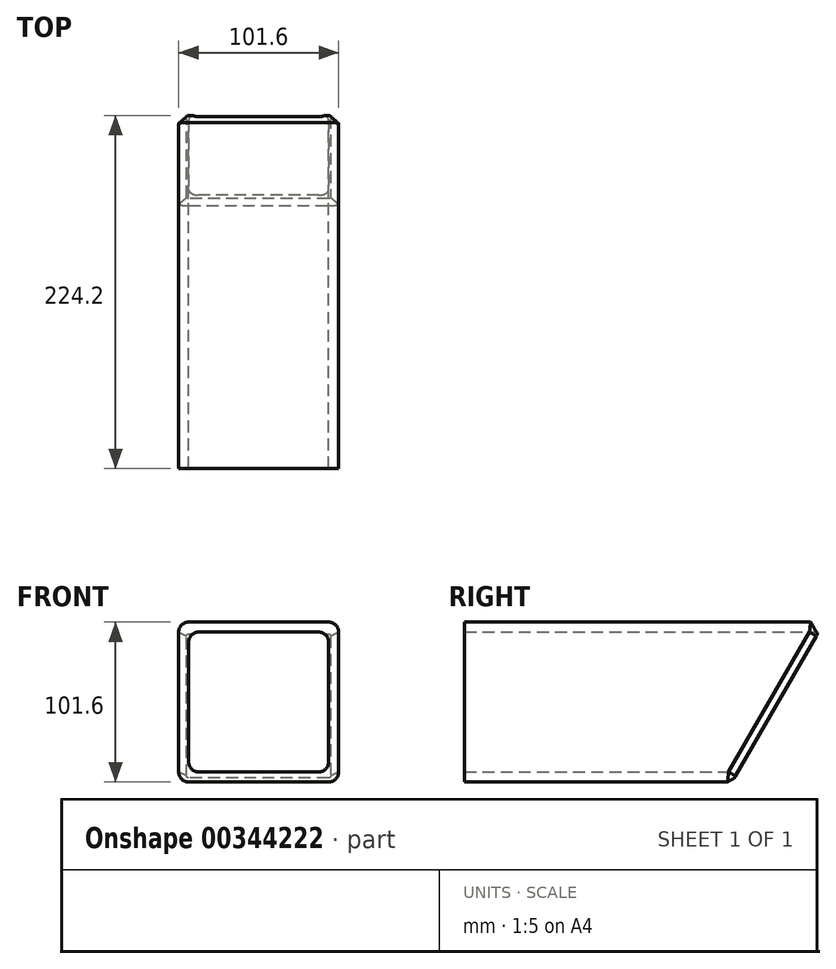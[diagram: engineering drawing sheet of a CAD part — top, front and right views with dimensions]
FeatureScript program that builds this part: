
annotation { "Feature Type Name" : "Feature", "Feature Type Description" : "" }
export const myFeature = defineFeature(function(context is Context, id is Id, definition is map)
    precondition{}
    {
        {
            var Q0;
            Q0=qCreatedBy(makeId("Front.planeOp"),FACE);
            var sketch = newSketch(context, id + "F0", { "sketchPlane" : qUnion([Q0])});
            skLineSegment(sketch, "E0.bottom", {"start": v(44.45, 50.8) * mm, "end": v(-44.45, 50.8) * mm});
            skLineSegment(sketch, "E0.top", {"start": v(44.45, -50.8) * mm, "end": v(-44.45, -50.8) * mm});
            skLineSegment(sketch, "E0.left", {"start": v(50.8, 44.45) * mm, "end": v(50.8, -44.45) * mm});
            skLineSegment(sketch, "E0.right", {"start": v(-50.8, 44.45) * mm, "end": v(-50.8, -44.45) * mm});
            skPoint(sketch, "E0.middle", {"position": v(0, 0) * mm});
            skPoint(sketch, "E1.visualSharp", {"position": v(-50.8, 50.8) * mm});
            skArc(sketch, "E1.filletArc", {"start": v(-44.45, 50.8) * mm, "mid": v(-48.94, 48.94) * mm, "end": v(-50.8, 44.45) * mm});
            skPoint(sketch, "E2.visualSharp", {"position": v(-50.8, -50.8) * mm});
            skArc(sketch, "E2.filletArc", {"start": v(-50.8, -44.45) * mm, "mid": v(-48.94, -48.94) * mm, "end": v(-44.45, -50.8) * mm});
            skPoint(sketch, "E3.visualSharp", {"position": v(50.8, 50.8) * mm});
            skArc(sketch, "E3.filletArc", {"start": v(50.8, 44.45) * mm, "mid": v(48.94, 48.94) * mm, "end": v(44.45, 50.8) * mm});
            skPoint(sketch, "E4.visualSharp", {"position": v(50.8, -50.8) * mm});
            skArc(sketch, "E4.filletArc", {"start": v(44.45, -50.8) * mm, "mid": v(48.94, -48.94) * mm, "end": v(50.8, -44.45) * mm});
            skLineSegment(sketch, "E5.bottom", {"start": v(38.1, 44.45) * mm, "end": v(-38.1, 44.45) * mm});
            skLineSegment(sketch, "E5.top", {"start": v(38.1, -44.45) * mm, "end": v(-38.1, -44.45) * mm});
            skLineSegment(sketch, "E5.left", {"start": v(44.45, 38.1) * mm, "end": v(44.45, -38.1) * mm});
            skLineSegment(sketch, "E5.right", {"start": v(-44.45, 38.1) * mm, "end": v(-44.45, -38.1) * mm});
            skArc(sketch, "E6.filletArc", {"start": v(-38.1, 44.45) * mm, "mid": v(-42.6, 42.6) * mm, "end": v(-44.45, 38.1) * mm});
            skArc(sketch, "E7.filletArc", {"start": v(44.45, 38.1) * mm, "mid": v(42.6, 42.6) * mm, "end": v(38.1, 44.45) * mm});
            skArc(sketch, "E8.filletArc", {"start": v(38.1, -44.45) * mm, "mid": v(42.6, -42.6) * mm, "end": v(44.45, -38.1) * mm});
            skArc(sketch, "E9.filletArc", {"start": v(-44.45, -38.1) * mm, "mid": v(-42.6, -42.6) * mm, "end": v(-38.1, -44.45) * mm});
            skSolve(sketch);
        }
        {
            var Q0;
            Q0=makeQuery(id+"F0.imprint","IMPRINT",FACE,{"disambiguationData":[TD([[makeQuery(id+"F0.imprint","IMPRINT",EDGE,{"derivedFrom":sQuery(id+"F0.wireOp",EDGE,"E0.bottom")}),1.0]])]});
            extrude(context, id + "F1", {"entities" : qUnion([Q0]), "depth" : 228.6 * mm});
        }
        {
            var Q0;
            Q0=makeQuery(id+"F1.opExtrude","SWEPT_FACE",FACE,{"disambiguationData":[OSD([sQuery(id+"F0.wireOp",EDGE,"E0.left")])]});
            var sketch = newSketch(context, id + "F2", { "sketchPlane" : qUnion([Q0])});
            skLineSegment(sketch, "E10.0", {"start": v(-228.6, -50.8) * mm, "end": v(0, -50.8) * mm});
            skPoint(sketch, "E11.0", {"position": v(0, 50.8) * mm});
            skLineSegment(sketch, "E12", {"start": v(0, 50.8) * mm, "end": v(0, -50.8) * mm});
            skLineSegment(sketch, "E13", {"start": v(0, 50.8) * mm, "end": v(-58.66, -50.8) * mm});
            skSolve(sketch);
        }
        {
            var Q0;
            Q0 = qSketchRegion(id + "F2", true);
            extrude(context, id + "F3", {"entities" : qUnion([Q0]), "operationType" : NewBodyOperationType.REMOVE, "endBound" : BoundingType.THROUGH_ALL, "oppositeDirection" : true, "depth" : 25.4 * mm});
        }
        {
            var Q0;
            Q0=makeQuery(id+"F3.boolean.opBoolean","COPY",EDGE,{"derivedFrom":makeQuery(id+"F3.opExtrude","CAP_EDGE",EDGE,{"disambiguationData":[OSD([sQuery(id+"F2.wireOp",EDGE,"E13")])],"isStart":true})});
            var Q1;
            Q1=makeQuery(id+"F3.boolean.opBoolean","INTERSECT",EDGE,{"derivedFrom":[makeQuery(id+"F1.opExtrude","SWEPT_FACE",FACE,{"disambiguationData":[OSD([sQuery(id+"F0.wireOp",EDGE,"E3.filletArc")])]}),makeQuery(id+"F3.opExtrude","SWEPT_FACE",FACE,{"disambiguationData":[OSD([sQuery(id+"F2.wireOp",EDGE,"E13")])]})]});
            chamfer(context, id + "F4", {"entities" : qUnion([Q0, Q1]), "width" : 5.08 * mm, "tangentPropagation" : true});
        }
    });
